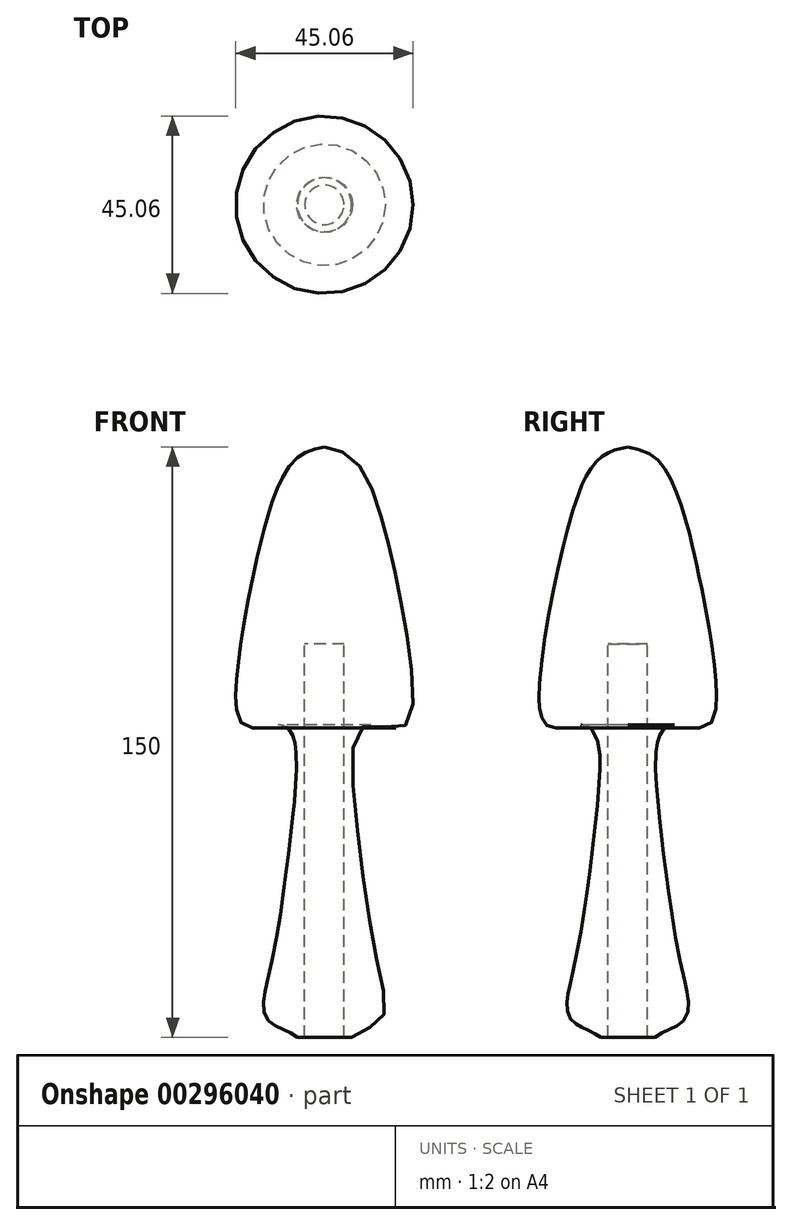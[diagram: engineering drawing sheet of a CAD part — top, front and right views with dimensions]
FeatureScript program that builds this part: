
annotation { "Feature Type Name" : "Feature", "Feature Type Description" : "" }
export const myFeature = defineFeature(function(context is Context, id is Id, definition is map)
    precondition{}
    {
        {
            var Q0;
            Q0=qCreatedBy(makeId("Front.planeOp"),FACE);
            var sketch = newSketch(context, id + "F0", { "sketchPlane" : qUnion([Q0])});
            skFitSpline(sketch, "E0", {"points": [v(6.86, 0) * mm, v(14.5, 4.6) * mm, v(13.6, 18.18) * mm, v(8, 56.7) * mm, v(10, 79) * mm, v(20, 78.88) * mm, v(22, 94.23) * mm, v(18.17, 116.94) * mm, v(13.98, 133.8) * mm, v(7.3, 146.95) * mm, v(0, 150) * mm], "startDerivative": vector(87.17, 68.86) * mm, "endDerivative": vector(-98.2, 16.76) * mm});
            skLineSegment(sketch, "E1", {"start": v(0, 0) * mm, "end": v(0, 150) * mm, "construction": true});
            skLineSegment(sketch, "E2", {"start": v(5, 0) * mm, "end": v(5, 100) * mm});
            skPoint(sketch, "E2.endSnap0", {"position": v(5, 0) * mm});
            skLineSegment(sketch, "E3", {"start": v(5, 100) * mm, "end": v(0, 100) * mm});
            skLineSegment(sketch, "E4", {"start": v(6.86, 0) * mm, "end": v(5, 0) * mm});
            skSolve(sketch);
        }
        {
            var Q0;
            Q0=sQuery(id+"F0.wireOp",EDGE,"E0");
            var Q1;
            Q1=sQuery(id+"F0.wireOp",EDGE,"E4");
            var Q2;
            Q2=sQuery(id+"F0.wireOp",EDGE,"E2");
            var Q3;
            Q3=sQuery(id+"F0.wireOp",EDGE,"E3");
            var Q4;
            Q4=sQuery(id+"F0.wireOp",EDGE,"E1");
            revolve(context, id + "F1", {"bodyType" : ToolBodyType.SURFACE, "surfaceEntities" : qUnion([Q0, Q1, Q2, Q3]), "axis" : qUnion([Q4]), "revolveType" : RevolveType.FULL});
        }
    });
